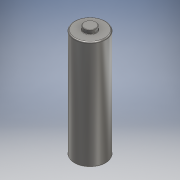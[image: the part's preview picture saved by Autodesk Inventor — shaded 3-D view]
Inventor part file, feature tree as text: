
AUTODESK INVENTOR PART (.ipt)
format: ipt  version: 2018 (Build 220112000, 112)  size: 123,904 bytes
history: native  units: mm
features: extrude x2, fillet x2, sketch x2, other x1
ambient origin geometry x8: Origin, YZ Plane, XZ Plane, XY Plane, X Axis, Y Axis, Z Axis, Center Point
bodies: Body1 (feature_tree)
feature tree (7):
  other  "ソリッド1"
  extrude  "押し出し1"  Depth=14.0mm
  extrude  "押し出し2"  Depth=48.5mm TaperAngle=0.0deg
  fillet  "フィレット1"  Radius=5.3mm
  fillet  "フィレット2"  Radius=1.7mm
  sketch  "スケッチ1"
  sketch  "スケッチ2"
